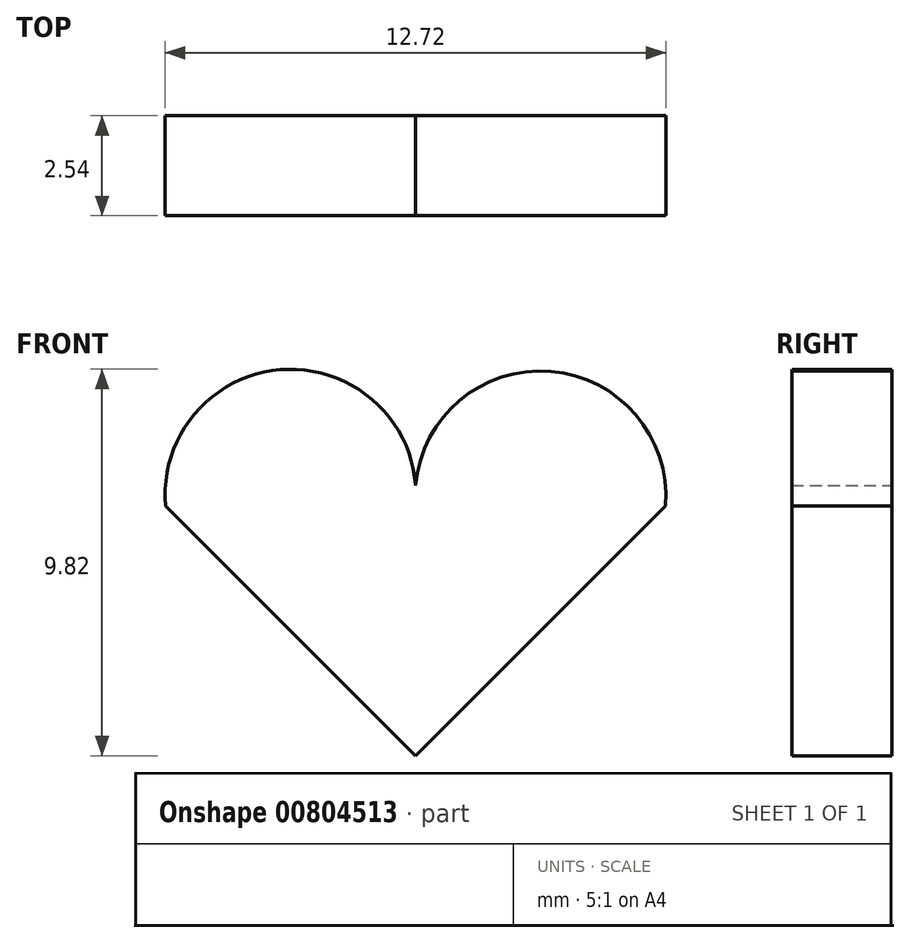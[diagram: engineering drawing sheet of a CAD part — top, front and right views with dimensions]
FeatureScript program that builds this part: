
annotation { "Feature Type Name" : "Feature", "Feature Type Description" : "" }
export const myFeature = defineFeature(function(context is Context, id is Id, definition is map)
    precondition{}
    {
        {
            var Q0;
            Q0=qCreatedBy(makeId("Front.planeOp"),FACE);
            var sketch = newSketch(context, id + "F0", { "sketchPlane" : qUnion([Q0])});
            skLineSegment(sketch, "E0.bottom", {"start": v(0, 0) * mm, "end": v(12.7, 0) * mm, "construction": true});
            skLineSegment(sketch, "E0.top", {"start": v(0, 12.7) * mm, "end": v(12.7, 12.7) * mm, "construction": true});
            skLineSegment(sketch, "E0.left", {"start": v(0, 0) * mm, "end": v(0, 12.7) * mm, "construction": true});
            skLineSegment(sketch, "E0.right", {"start": v(12.7, 0) * mm, "end": v(12.7, 12.7) * mm, "construction": true});
            skLineSegment(sketch, "E1", {"start": v(6.35, 0) * mm, "end": v(12.7, 6.35) * mm, "construction": true});
            skLineSegment(sketch, "E2", {"start": v(6.35, 0) * mm, "end": v(0, 6.35) * mm, "construction": true});
            skArc(sketch, "E3", {"start": v(6.35, 6.35) * mm, "mid": v(3.17, 9.85) * mm, "end": v(0, 6.35) * mm, "construction": true});
            skArc(sketch, "E4", {"start": v(12.7, 6.35) * mm, "mid": v(9.52, 9.78) * mm, "end": v(6.35, 6.35) * mm, "construction": true});
            skLineSegment(sketch, "E5", {"start": v(0, 6.35) * mm, "end": v(6.35, 0) * mm});
            skLineSegment(sketch, "E6", {"start": v(6.35, 0) * mm, "end": v(12.7, 6.35) * mm});
            skArc(sketch, "E7", {"start": v(6.35, 6.35) * mm, "mid": v(3.17, 9.82) * mm, "end": v(0, 6.35) * mm});
            skArc(sketch, "E8", {"start": v(12.7, 6.35) * mm, "mid": v(9.52, 9.78) * mm, "end": v(6.35, 6.35) * mm});
            skSolve(sketch);
        }
        {
            var Q0;
            Q0 = qSketchRegion(id + "F0", true);
            extrude(context, id + "F1", {"entities" : qUnion([Q0]), "depth" : 2.54 * mm, "offsetDistance" : 25.4 * mm});
        }
    });
